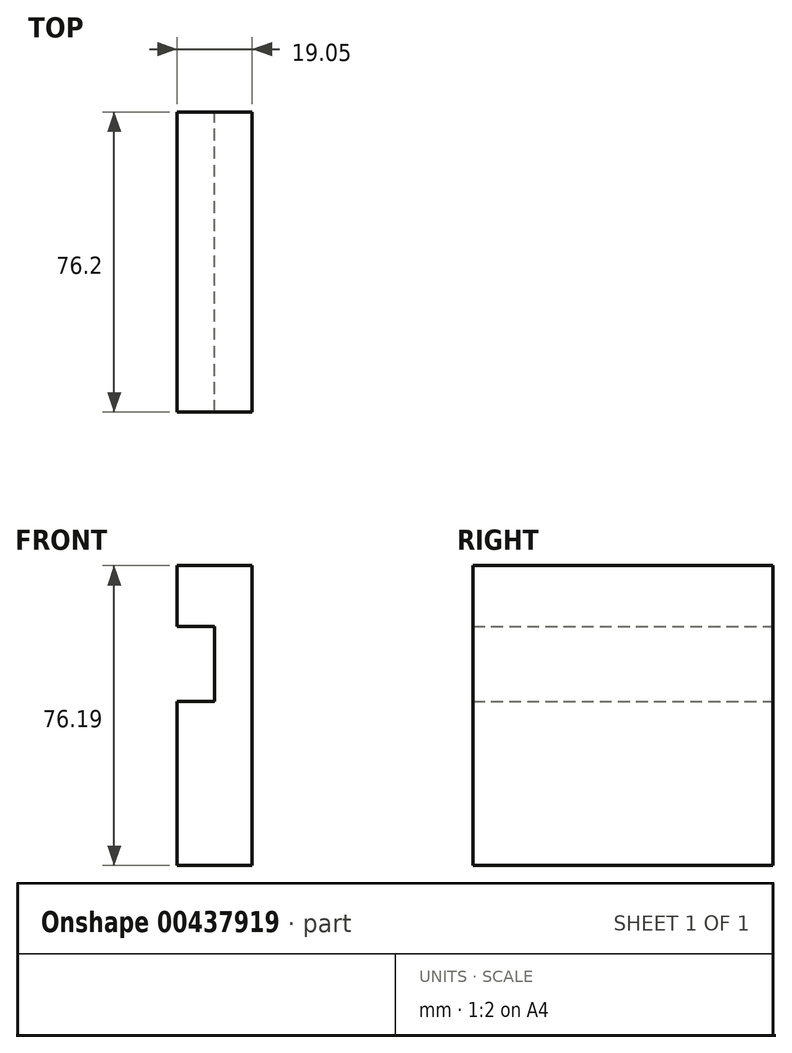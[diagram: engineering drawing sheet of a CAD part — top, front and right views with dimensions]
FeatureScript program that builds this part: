
annotation { "Feature Type Name" : "Feature", "Feature Type Description" : "" }
export const myFeature = defineFeature(function(context is Context, id is Id, definition is map)
    precondition{}
    {
        {
            var Q0;
            Q0=qCreatedBy(makeId("Front.planeOp"),FACE);
            var sketch = newSketch(context, id + "F0", { "sketchPlane" : qUnion([Q0])});
            skLineSegment(sketch, "E0", {"start": v(0, 0) * mm, "end": v(-19.05, 0) * mm});
            skLineSegment(sketch, "E1", {"start": v(0, 0) * mm, "end": v(0, 76.2) * mm});
            skLineSegment(sketch, "E2", {"start": v(0, 76.2) * mm, "end": v(-19.05, 76.2) * mm});
            skLineSegment(sketch, "E3", {"start": v(-19.05, 76.2) * mm, "end": v(-19.05, 60.72) * mm});
            skLineSegment(sketch, "E4", {"start": v(-19.05, 60.72) * mm, "end": v(-9.52, 60.72) * mm});
            skLineSegment(sketch, "E5", {"start": v(-9.52, 60.72) * mm, "end": v(-9.52, 41.67) * mm});
            skLineSegment(sketch, "E6", {"start": v(-9.52, 41.67) * mm, "end": v(-19.05, 41.67) * mm});
            skLineSegment(sketch, "E7", {"start": v(-19.05, 41.67) * mm, "end": v(-19.05, 0) * mm});
            skSolve(sketch);
        }
        {
            var Q0;
            Q0 = qSketchRegion(id + "F0", true);
            extrude(context, id + "F1", {"entities" : qUnion([Q0]), "depth" : 76.2 * mm});
        }
    });
